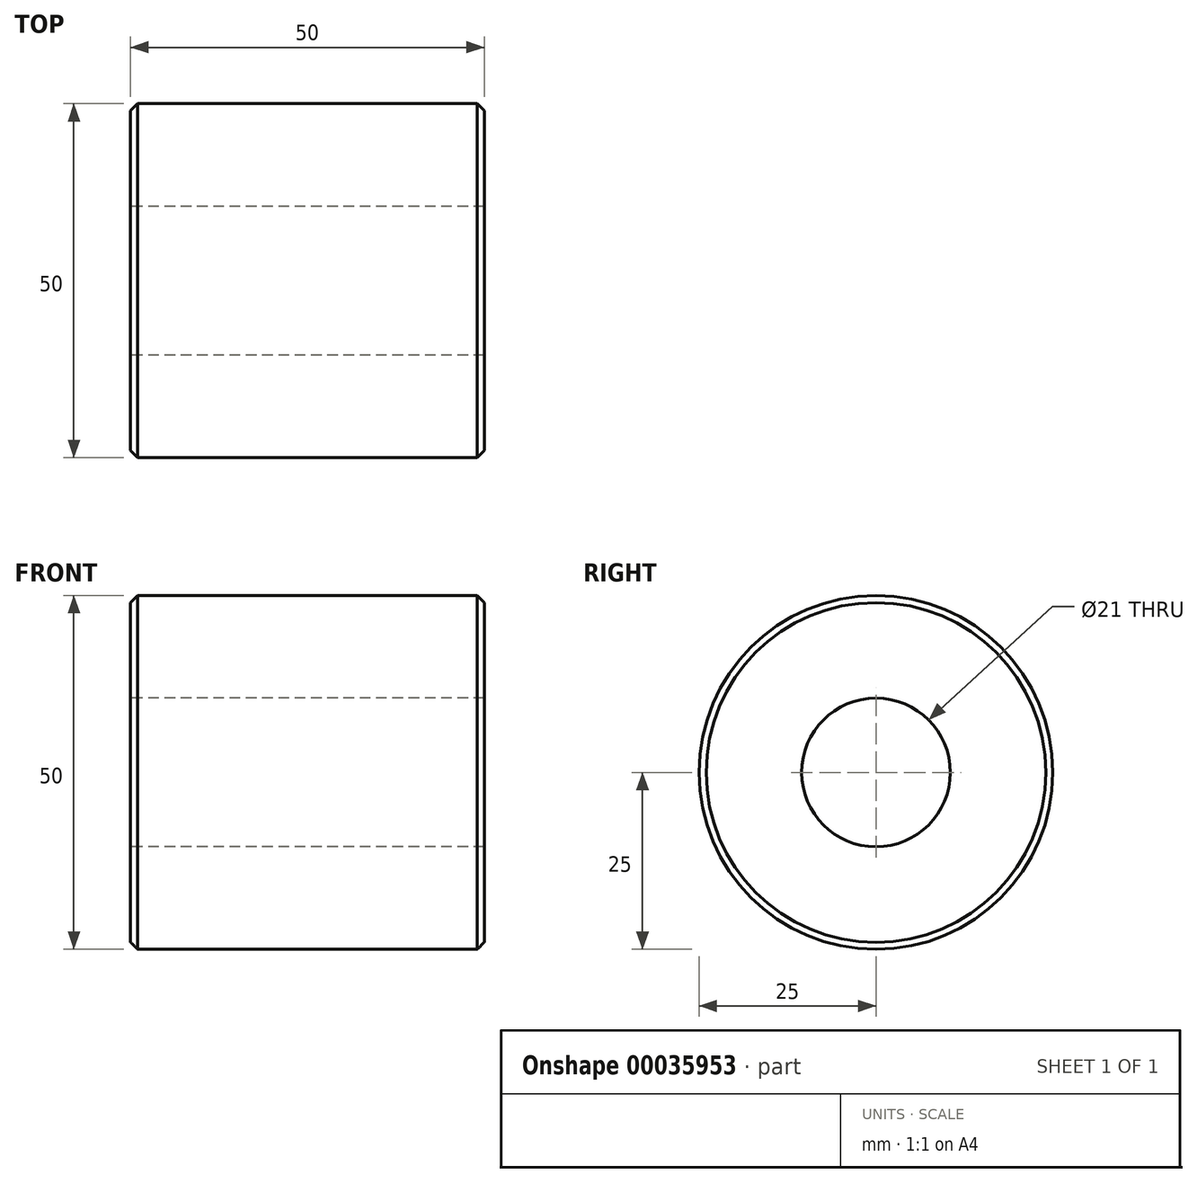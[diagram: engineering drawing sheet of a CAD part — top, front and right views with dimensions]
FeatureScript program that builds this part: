
annotation { "Feature Type Name" : "Feature", "Feature Type Description" : "" }
export const myFeature = defineFeature(function(context is Context, id is Id, definition is map)
    precondition{}
    {
        {
            var Q0;
            Q0=qCreatedBy(makeId("Right.planeOp"),FACE);
            var sketch = newSketch(context, id + "F0", { "sketchPlane" : qUnion([Q0])});
            skCircle(sketch, "E0", {"center": v(0, 0) * mm, "radius": 10.5 * mm});
            skCircle(sketch, "E1", {"center": v(0, 0) * mm, "radius": 25 * mm});
            skSolve(sketch);
        }
        {
            var Q0;
            Q0=makeQuery(id+"F0.imprint","IMPRINT",FACE,{"disambiguationData":[TD([[makeQuery(id+"F0.imprint","IMPRINT",EDGE,{"derivedFrom":sQuery(id+"F0.wireOp",EDGE,"E0")}),-1.0]])]});
            extrude(context, id + "F1", {"entities" : qUnion([Q0]), "depth" : 50 * mm});
        }
        {
            var Q0;
            Q0=makeQuery(id+"F1.opExtrude","CAP_EDGE",EDGE,{"disambiguationData":[OSD([sQuery(id+"F0.wireOp",EDGE,"E1")])],"isStart":false});
            var Q1;
            Q1=makeQuery(id+"F1.opExtrude","CAP_EDGE",EDGE,{"disambiguationData":[OSD([sQuery(id+"F0.wireOp",EDGE,"E1")])],"isStart":true});
            chamfer(context, id + "F2", {"entities" : qUnion([Q0, Q1]), "width" : 1 * mm, "tangentPropagation" : true});
        }
    });
